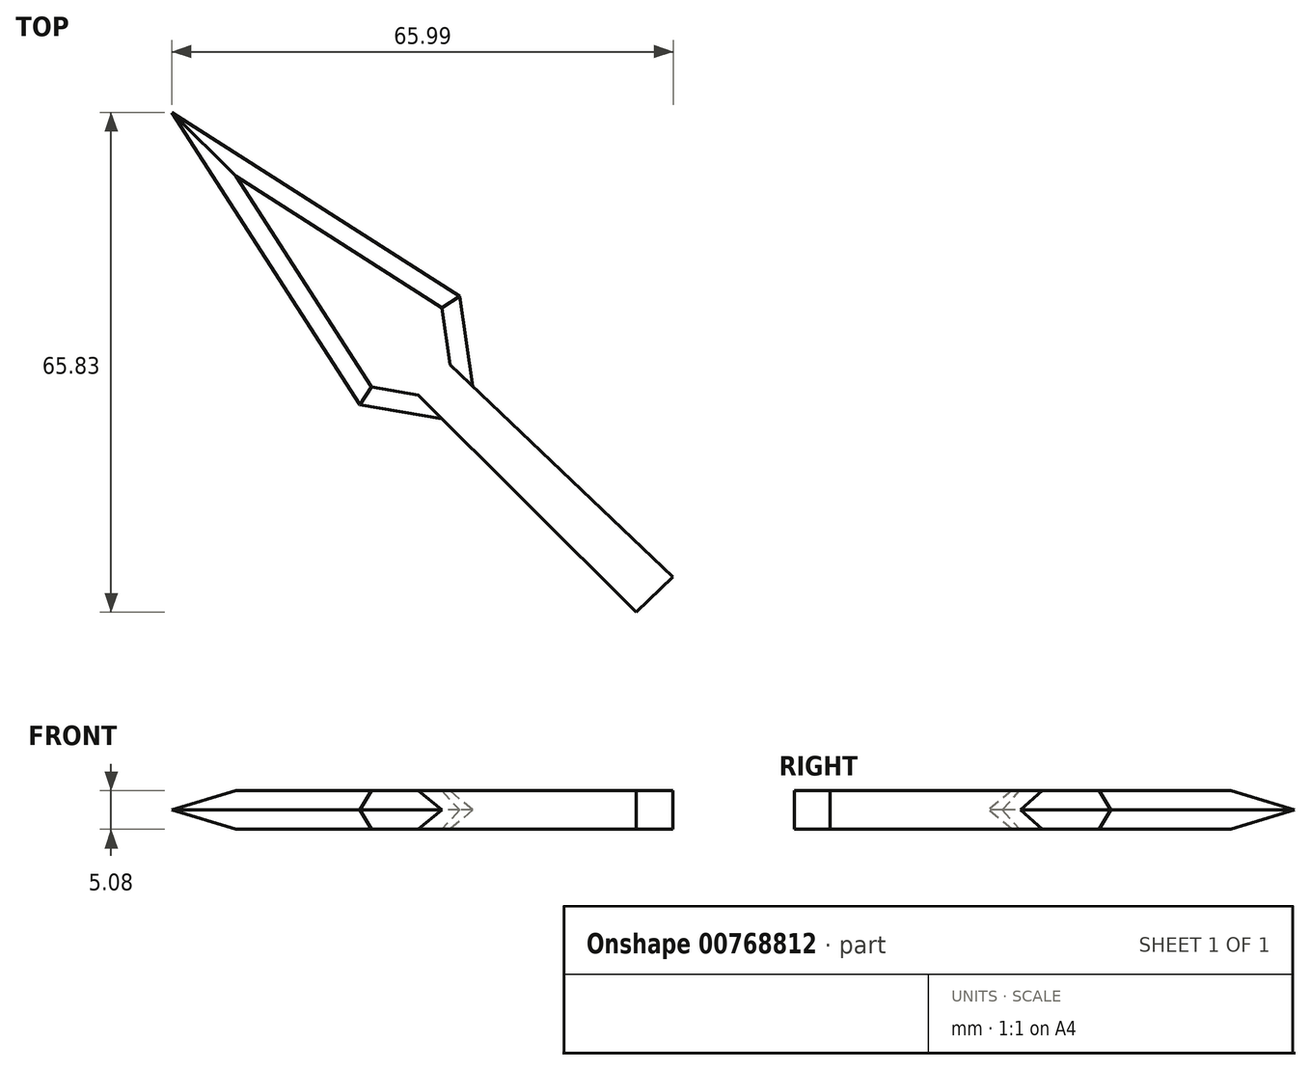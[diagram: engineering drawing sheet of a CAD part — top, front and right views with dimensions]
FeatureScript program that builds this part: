
annotation { "Feature Type Name" : "Feature", "Feature Type Description" : "" }
export const myFeature = defineFeature(function(context is Context, id is Id, definition is map)
    precondition{}
    {
        {
            var Q0;
            Q0=qCreatedBy(makeId("Top.planeOp"),FACE);
            var sketch = newSketch(context, id + "F0", { "sketchPlane" : qUnion([Q0])});
            skLineSegment(sketch, "E0", {"start": v(-51, 47.32) * mm, "end": v(-19.38, -1.9) * mm});
            skLineSegment(sketch, "E1", {"start": v(-19.38, -1.9) * mm, "end": v(-3.92, -4.52) * mm});
            skLineSegment(sketch, "E2", {"start": v(-3.92, -4.52) * mm, "end": v(18.53, -26.91) * mm});
            skLineSegment(sketch, "E3", {"start": v(23.4, -22.26) * mm, "end": v(0, 0) * mm});
            skLineSegment(sketch, "E4", {"start": v(0, 0) * mm, "end": v(-2.37, 16.2) * mm});
            skLineSegment(sketch, "E5", {"start": v(-2.37, 16.2) * mm, "end": v(-51, 47.32) * mm});
            skLineSegment(sketch, "E6", {"start": v(18.53, -26.91) * mm, "end": v(23.4, -22.26) * mm});
            skSolve(sketch);
        }
        {
            var Q0;
            Q0=qCreatedBy(makeId("Front.planeOp"),FACE);
            var sketch = newSketch(context, id + "F1", { "sketchPlane" : qUnion([Q0])});
            skCircle(sketch, "E7", {"center": v(18.64, 0) * mm, "radius": 3.3 * mm});
            skSolve(sketch);
        }
        {
            var Q0;
            Q0=qCreatedBy(makeId("Front.planeOp"),FACE);
            var sketch = newSketch(context, id + "F2", { "sketchPlane" : qUnion([Q0])});
            skLineSegment(sketch, "E8", {"start": v(27.67, 11.68) * mm, "end": v(27.67, -12.59) * mm});
            skSolve(sketch);
        }
        {
            var Q0;
            Q0=sQuery(id+"F1.wireOp",EDGE,"E7");
            var Q1;
            Q1=sQuery(id+"F2.wireOp",EDGE,"E8");
            revolve(context, id + "F3", {"bodyType" : ToolBodyType.SURFACE, "surfaceOperationType" : NewSurfaceOperationType.NEW, "surfaceEntities" : qUnion([Q0]), "axis" : qUnion([Q1]), "revolveType" : RevolveType.FULL});
        }
        {
            var Q0;
            Q0 = qSketchRegion(id + "F0", true);
            extrude(context, id + "F4", {"entities" : qUnion([Q0]), "depth" : 5.08 * mm, "offsetDistance" : 25.4 * mm});
        }
        {
            var Q0;
            Q0=makeQuery(id+"F4.opExtrude","CAP_EDGE",EDGE,{"disambiguationData":[OSD([sQuery(id+"F0.wireOp",EDGE,"E1")])],"isStart":true});
            var Q1;
            Q1=makeQuery(id+"F4.opExtrude","CAP_EDGE",EDGE,{"disambiguationData":[OSD([sQuery(id+"F0.wireOp",EDGE,"E0")])],"isStart":true});
            var Q2;
            Q2=makeQuery(id+"F4.opExtrude","CAP_EDGE",EDGE,{"disambiguationData":[OSD([sQuery(id+"F0.wireOp",EDGE,"E5")])],"isStart":true});
            var Q3;
            Q3=makeQuery(id+"F4.opExtrude","CAP_EDGE",EDGE,{"disambiguationData":[OSD([sQuery(id+"F0.wireOp",EDGE,"E4")])],"isStart":true});
            chamfer(context, id + "F5", {"entities" : qUnion([Q0, Q1, Q2, Q3]), "chamferType" : ChamferType.OFFSET_ANGLE, "width" : 5.08 * mm, "oppositeDirection" : false, "angle" : 45 * degree, "tangentPropagation" : true});
        }
        {
            var Q0;
            {var subQ0=sQuery(id+"F0.wireOp",EDGE,"E0");Q0=makeQuery(id+"F5.opChamfer","BLEND_EDGE",EDGE,{"blendedFrom":[makeQuery(id+"F4.opExtrude","CAP_EDGE",EDGE,{"disambiguationData":[OSD([subQ0])],"isStart":true}),makeQuery(id+"F4.opExtrude","CAP_FACE",FACE,{"disambiguationData":[OSD([subQ0,sQuery(id+"F0.wireOp",EDGE,"E1"),sQuery(id+"F0.wireOp",EDGE,"E2"),sQuery(id+"F0.wireOp",EDGE,"E3"),sQuery(id+"F0.wireOp",EDGE,"E4"),sQuery(id+"F0.wireOp",EDGE,"E5"),sQuery(id+"F0.wireOp",EDGE,"E6")])],"isStart":false})],"blendedInto":[makeQuery(id+"F4.opExtrude","CAP_FACE",FACE,{"disambiguationData":[OSD([subQ0,sQuery(id+"F0.wireOp",EDGE,"E1"),sQuery(id+"F0.wireOp",EDGE,"E2"),sQuery(id+"F0.wireOp",EDGE,"E3"),sQuery(id+"F0.wireOp",EDGE,"E4"),sQuery(id+"F0.wireOp",EDGE,"E5"),sQuery(id+"F0.wireOp",EDGE,"E6")])],"isStart":false})]});}
            var Q1;
            {var subQ0=sQuery(id+"F0.wireOp",EDGE,"E5");Q1=makeQuery(id+"F5.opChamfer","BLEND_EDGE",EDGE,{"blendedFrom":[makeQuery(id+"F4.opExtrude","CAP_EDGE",EDGE,{"disambiguationData":[OSD([subQ0])],"isStart":true}),makeQuery(id+"F4.opExtrude","CAP_FACE",FACE,{"disambiguationData":[OSD([sQuery(id+"F0.wireOp",EDGE,"E0"),sQuery(id+"F0.wireOp",EDGE,"E1"),sQuery(id+"F0.wireOp",EDGE,"E2"),sQuery(id+"F0.wireOp",EDGE,"E3"),sQuery(id+"F0.wireOp",EDGE,"E4"),subQ0,sQuery(id+"F0.wireOp",EDGE,"E6")])],"isStart":false})],"blendedInto":[makeQuery(id+"F4.opExtrude","CAP_FACE",FACE,{"disambiguationData":[OSD([sQuery(id+"F0.wireOp",EDGE,"E0"),sQuery(id+"F0.wireOp",EDGE,"E1"),sQuery(id+"F0.wireOp",EDGE,"E2"),sQuery(id+"F0.wireOp",EDGE,"E3"),sQuery(id+"F0.wireOp",EDGE,"E4"),subQ0,sQuery(id+"F0.wireOp",EDGE,"E6")])],"isStart":false})]});}
            var Q2;
            {var subQ0=sQuery(id+"F0.wireOp",EDGE,"E4");Q2=makeQuery(id+"F5.opChamfer","BLEND_EDGE",EDGE,{"blendedFrom":[makeQuery(id+"F4.opExtrude","CAP_EDGE",EDGE,{"disambiguationData":[OSD([subQ0])],"isStart":true}),makeQuery(id+"F4.opExtrude","CAP_FACE",FACE,{"disambiguationData":[OSD([sQuery(id+"F0.wireOp",EDGE,"E0"),sQuery(id+"F0.wireOp",EDGE,"E1"),sQuery(id+"F0.wireOp",EDGE,"E2"),sQuery(id+"F0.wireOp",EDGE,"E3"),subQ0,sQuery(id+"F0.wireOp",EDGE,"E5"),sQuery(id+"F0.wireOp",EDGE,"E6")])],"isStart":false})],"blendedInto":[makeQuery(id+"F4.opExtrude","CAP_FACE",FACE,{"disambiguationData":[OSD([sQuery(id+"F0.wireOp",EDGE,"E0"),sQuery(id+"F0.wireOp",EDGE,"E1"),sQuery(id+"F0.wireOp",EDGE,"E2"),sQuery(id+"F0.wireOp",EDGE,"E3"),subQ0,sQuery(id+"F0.wireOp",EDGE,"E5"),sQuery(id+"F0.wireOp",EDGE,"E6")])],"isStart":false})]});}
            var Q3;
            {var subQ0=sQuery(id+"F0.wireOp",EDGE,"E1");Q3=makeQuery(id+"F5.opChamfer","BLEND_EDGE",EDGE,{"blendedFrom":[makeQuery(id+"F4.opExtrude","CAP_EDGE",EDGE,{"disambiguationData":[OSD([subQ0])],"isStart":true}),makeQuery(id+"F4.opExtrude","CAP_FACE",FACE,{"disambiguationData":[OSD([sQuery(id+"F0.wireOp",EDGE,"E0"),subQ0,sQuery(id+"F0.wireOp",EDGE,"E2"),sQuery(id+"F0.wireOp",EDGE,"E3"),sQuery(id+"F0.wireOp",EDGE,"E4"),sQuery(id+"F0.wireOp",EDGE,"E5"),sQuery(id+"F0.wireOp",EDGE,"E6")])],"isStart":false})],"blendedInto":[makeQuery(id+"F4.opExtrude","CAP_FACE",FACE,{"disambiguationData":[OSD([sQuery(id+"F0.wireOp",EDGE,"E0"),subQ0,sQuery(id+"F0.wireOp",EDGE,"E2"),sQuery(id+"F0.wireOp",EDGE,"E3"),sQuery(id+"F0.wireOp",EDGE,"E4"),sQuery(id+"F0.wireOp",EDGE,"E5"),sQuery(id+"F0.wireOp",EDGE,"E6")])],"isStart":false})]});}
            chamfer(context, id + "F6", {"entities" : qUnion([Q0, Q1, Q2, Q3]), "chamferType" : ChamferType.OFFSET_ANGLE, "width" : 5.08 * mm, "oppositeDirection" : false, "angle" : 45 * degree, "tangentPropagation" : true});
        }
    });
